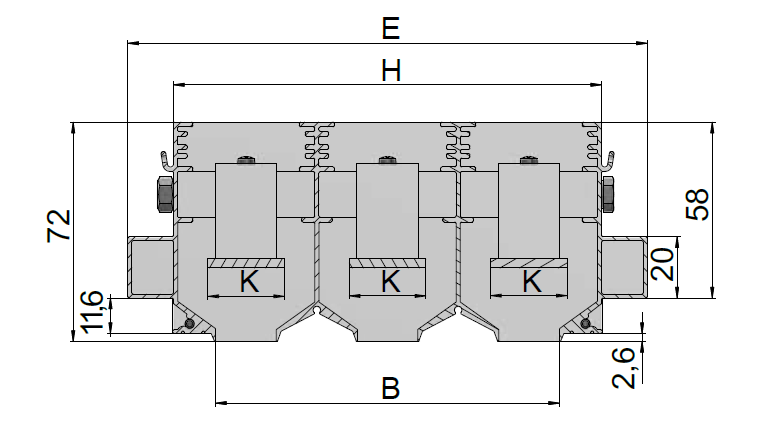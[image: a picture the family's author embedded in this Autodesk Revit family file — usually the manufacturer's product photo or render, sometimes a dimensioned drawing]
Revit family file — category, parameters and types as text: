
# Revit family: GR_Адаптер линейный_Муфта(n)_АДЛ-КСД-У_П_R21
name_source: partatom
category: Соединительные детали воздуховодов
units: mm (PartAtom-declared; Revit-internal decimal feet)

## family parameters
Всегда вертикально = Да
Заголовок OmniClass = Metal Ducts
На основе рабочей плоскости = Нет
Номер OmniClass = 23.75.70.14.31
Общий = Нет
При загрузке вырезать с полостями = Нет
Размер круглого соединителя = Использовать диаметр
Тип детали = Мультипорт

## types (6) — shared parameters
ADSK_URL страницы изделия = https://grilles.ru
ADSK_Версия Revit = 2021
ADSK_Единица измерения = шт.
ADSK_Завод-изготовитель = ООО "ВЕНТРЕШЕТКИКОМ"
ADSK_Код изделия = 002010
ADSK_Количество = 1
ADSK_Материал = ADSK_Оцинкованная сталь
ADSK_Наименование = АДЛ-КСД-У-П, адаптер вентиляционной решётки радиальный
Изготовитель = ООО "ВЕНТРЕШЕТКИКОМ"
Корпус_Металл_Толщина = 1 мм
Муфта_Металл_Толщина = 1 мм
zero-valued in all types: Отметка по умолчанию

## per-type parameters (varying)
| type | Корпус_Высота | Корпус_Длина | Решетка_отступ | Решётка_Высота |
| АДЛ-КСД-У-П 1-20 | 75 мм | 171 мм | 25 мм | 48 мм |
| АДЛ-КСД-У-П 2-20 | 105 мм | 209 мм | 44 мм | 86 мм |
| АДЛ-КСД-У-П 3-20 | 105 мм | 247 мм | 63 мм | 124 мм |
| АДЛ-КСД-У-П 4-20 | 140 мм | 285 мм | 82 мм | 162 мм |
| АДЛ-КСД-У-П 5-20 | 140 мм | 323 мм | 101 мм | 200 мм |
| АДЛ-КСД-У-П 6-20 | 175 мм | 361 мм | 120 мм | 238 мм |

note: column(s) folded — value = type name in every type: ADSK_Марка
